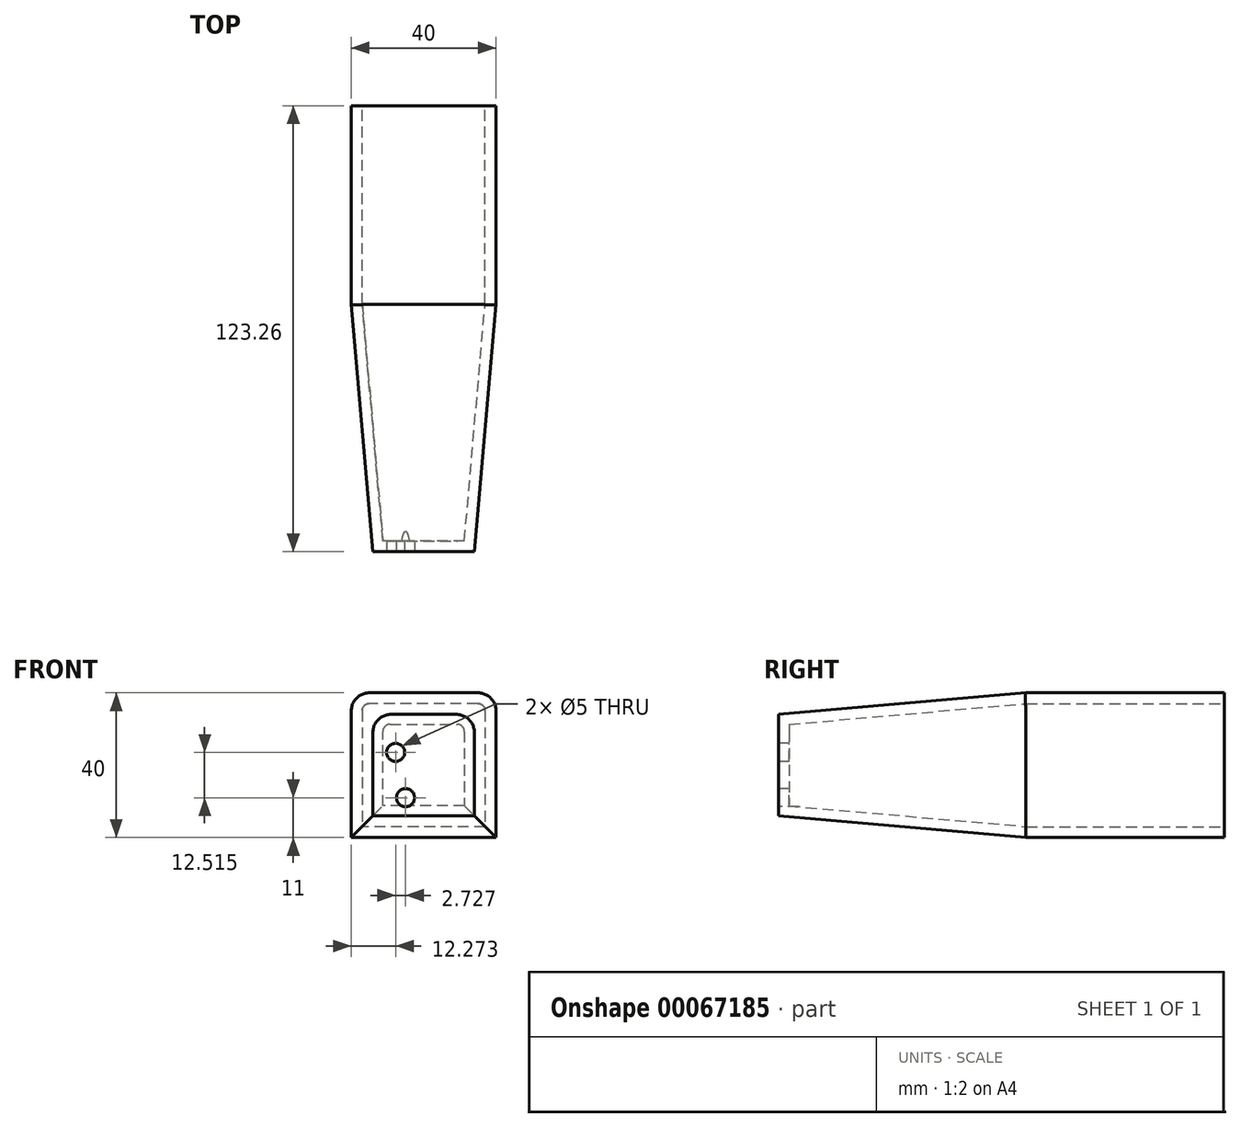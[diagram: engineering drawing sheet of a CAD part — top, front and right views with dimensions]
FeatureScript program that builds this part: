
annotation { "Feature Type Name" : "Feature", "Feature Type Description" : "" }
export const myFeature = defineFeature(function(context is Context, id is Id, definition is map)
    precondition{}
    {
        {
            var Q0;
            Q0=qCreatedBy(makeId("Front.planeOp"),FACE);
            var sketch = newSketch(context, id + "F0", { "sketchPlane" : qUnion([Q0])});
            skLineSegment(sketch, "E0.rect.bottom", {"start": v(20, 20) * mm, "end": v(-20, 20) * mm});
            skLineSegment(sketch, "E0.rect.top", {"start": v(20, -20) * mm, "end": v(-20, -20) * mm});
            skLineSegment(sketch, "E0.rect.left", {"start": v(20, 20) * mm, "end": v(20, -20) * mm});
            skLineSegment(sketch, "E0.rect.right", {"start": v(-20, 20) * mm, "end": v(-20, -20) * mm});
            skPoint(sketch, "E0.rect.middle", {"position": v(0, 0) * mm});
            skSolve(sketch);
        }
        {
            var Q0;
            Q0=makeQuery(id+"F0.imprint","IMPRINT",FACE,{"disambiguationData":[TD([[makeQuery(id+"F0.imprint","IMPRINT",EDGE,{"derivedFrom":sQuery(id+"F0.wireOp",EDGE,"E0.rect.bottom")}),1.0]])]});
            extrude(context, id + "F1", {"entities" : qUnion([Q0]), "depth" : 68.34 * mm, "hasDraft" : true, "draftAngle" : 5 * degree, "draftPullDirection" : true, "hasSecondDirection" : true, "secondDirectionOppositeDirection" : true, "secondDirectionDepth" : 54.92 * mm});
        }
        {
            var Q0;
            Q0=makeQuery(id+"F1.split0.splitOp","SPLIT",EDGE,{"derivedFrom":makeQuery(id+"F1.opExtrude","SWEPT_EDGE",EDGE,{"disambiguationData":[OSD([sQuery(id+"F0.wireOp",EDGE,"E0.rect.bottom"),sQuery(id+"F0.wireOp",EDGE,"E0.rect.left")])]})});
            var Q1;
            Q1=makeQuery(id+"F1.split0.splitOp","SPLIT",EDGE,{"derivedFrom":makeQuery(id+"F1.opExtrude","SWEPT_EDGE",EDGE,{"disambiguationData":[OSD([sQuery(id+"F0.wireOp",EDGE,"E0.rect.bottom"),sQuery(id+"F0.wireOp",EDGE,"E0.rect.left")])]}),"isFromBackBody":true});
            var Q2;
            Q2=makeQuery(id+"F1.split0.splitOp","SPLIT",EDGE,{"derivedFrom":makeQuery(id+"F1.opExtrude","SWEPT_EDGE",EDGE,{"disambiguationData":[OSD([sQuery(id+"F0.wireOp",EDGE,"E0.rect.bottom"),sQuery(id+"F0.wireOp",EDGE,"E0.rect.right")])]}),"isFromBackBody":true});
            var Q3;
            Q3=makeQuery(id+"F1.split0.splitOp","SPLIT",EDGE,{"derivedFrom":makeQuery(id+"F1.opExtrude","SWEPT_EDGE",EDGE,{"disambiguationData":[OSD([sQuery(id+"F0.wireOp",EDGE,"E0.rect.bottom"),sQuery(id+"F0.wireOp",EDGE,"E0.rect.right")])]})});
            fillet(context, id + "F2", {"entities" : qUnion([Q0, Q1, Q2, Q3]), "radius" : 5 * mm, "tangentPropagation" : true, "allowEdgeOverflow" : false});
        }
        {
            var Q0;
            Q0=makeQuery(id+"F1.opExtrude","CAP_FACE",FACE,{"disambiguationData":[OSD([sQuery(id+"F0.wireOp",EDGE,"E0.rect.bottom"),sQuery(id+"F0.wireOp",EDGE,"E0.rect.top"),sQuery(id+"F0.wireOp",EDGE,"E0.rect.left"),sQuery(id+"F0.wireOp",EDGE,"E0.rect.right")])],"isStart":true});
            var Q1;
            Q1=makeQuery(id+"F1.split0.splitOp","SPLIT",BODY,{"derivedFrom":makeQuery(id+"F1.opExtrude","SWEPT_BODY",BODY,{"disambiguationData":[OSD([sQuery(id+"F0.wireOp",EDGE,"E0.rect.bottom"),sQuery(id+"F0.wireOp",EDGE,"E0.rect.top"),sQuery(id+"F0.wireOp",EDGE,"E0.rect.left"),sQuery(id+"F0.wireOp",EDGE,"E0.rect.right")])]})});
            shell(context, id + "F3", {"entities" : qUnion([Q0]), "parts" : qUnion([Q1]), "thickness" : 3 * mm});
        }
        {
            var Q0;
            Q0=makeQuery(id+"F1.opExtrude","CAP_FACE",FACE,{"disambiguationData":[OSD([sQuery(id+"F0.wireOp",EDGE,"E0.rect.bottom"),sQuery(id+"F0.wireOp",EDGE,"E0.rect.top"),sQuery(id+"F0.wireOp",EDGE,"E0.rect.left"),sQuery(id+"F0.wireOp",EDGE,"E0.rect.right")])],"isStart":false});
            var sketch = newSketch(context, id + "F4", { "sketchPlane" : qUnion([Q0])});
            skPoint(sketch, "E1", {"position": v(-7.73, 3.52) * mm});
            skPoint(sketch, "E2", {"position": v(-5, -9) * mm});
            skSolve(sketch);
        }
        {
            var Q0;
            Q0=sQuery(id+"F4.wireOp",VERTEX,"E2");
            var Q1;
            Q1=sQuery(id+"F4.wireOp",VERTEX,"E1");
            var Q2;
            Q2=makeQuery(id+"F1.split0.splitOp","SPLIT",BODY,{"derivedFrom":makeQuery(id+"F1.opExtrude","SWEPT_BODY",BODY,{"disambiguationData":[OSD([sQuery(id+"F0.wireOp",EDGE,"E0.rect.bottom"),sQuery(id+"F0.wireOp",EDGE,"E0.rect.top"),sQuery(id+"F0.wireOp",EDGE,"E0.rect.left"),sQuery(id+"F0.wireOp",EDGE,"E0.rect.right")])]})});
            hole(context, id + "F5", {"style" : HoleStyle.SIMPLE, "holeDiameter" : 5 * mm, "endStyle" : HoleEndStyle.THROUGH, "locations" : qUnion([Q0, Q1]), "scope" : qUnion([Q2])});
        }
    });
